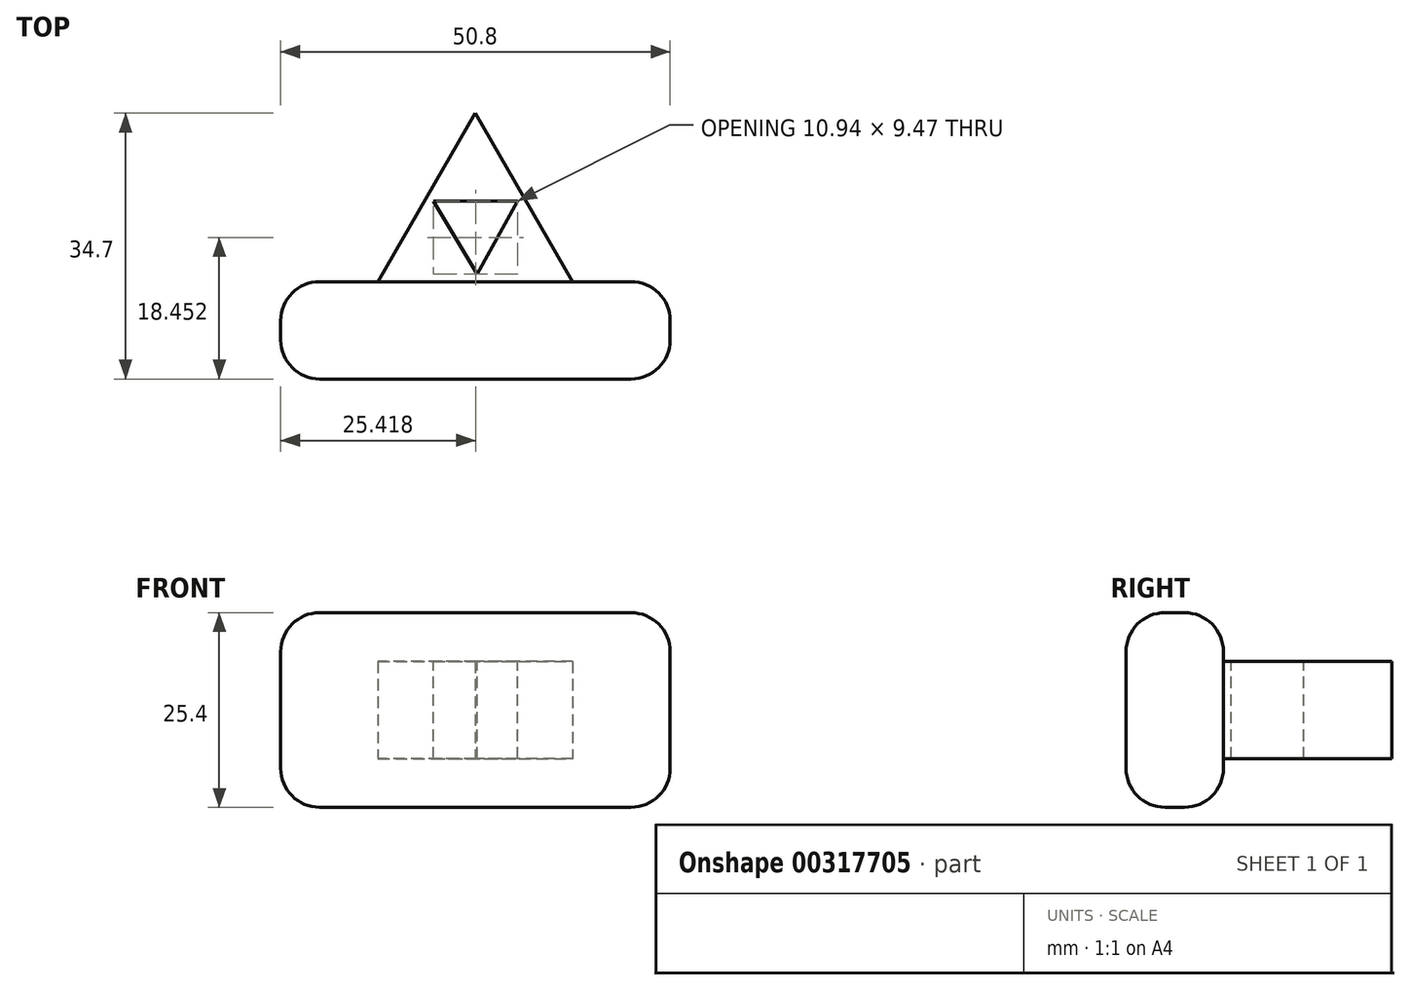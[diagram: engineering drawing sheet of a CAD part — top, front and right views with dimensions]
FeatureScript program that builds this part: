
annotation { "Feature Type Name" : "Feature", "Feature Type Description" : "" }
export const myFeature = defineFeature(function(context is Context, id is Id, definition is map)
    precondition{}
    {
        {
            var Q0;
            Q0=qCreatedBy(makeId("Top.planeOp"),FACE);
            var sketch = newSketch(context, id + "F0", { "sketchPlane" : qUnion([Q0])});
            skLineSegment(sketch, "E0", {"start": v(-12.7, -2.56) * mm, "end": v(12.7, -2.56) * mm});
            skLineSegment(sketch, "E1", {"start": v(12.7, -2.56) * mm, "end": v(0, 19.44) * mm});
            skLineSegment(sketch, "E2", {"start": v(0, 19.44) * mm, "end": v(-12.7, -2.56) * mm});
            skLineSegment(sketch, "E3", {"start": v(-12.7, -2.56) * mm, "end": v(-25.4, -2.56) * mm});
            skLineSegment(sketch, "E4", {"start": v(12.7, -2.56) * mm, "end": v(0.27, -2.56) * mm});
            skLineSegment(sketch, "E5", {"start": v(12.7, -2.56) * mm, "end": v(25.4, -2.56) * mm});
            skLineSegment(sketch, "E6", {"start": v(25.4, -2.56) * mm, "end": v(25.4, -15.26) * mm});
            skLineSegment(sketch, "E7", {"start": v(25.4, -15.26) * mm, "end": v(-25.4, -15.26) * mm});
            skLineSegment(sketch, "E8", {"start": v(-25.4, -15.26) * mm, "end": v(-25.4, -2.56) * mm});
            skLineSegment(sketch, "E9", {"start": v(0.27, -2.56) * mm, "end": v(-6.35, 8.44) * mm});
            skLineSegment(sketch, "E10", {"start": v(-6.35, 8.44) * mm, "end": v(6.35, 8.44) * mm});
            skLineSegment(sketch, "E11", {"start": v(6.35, 8.44) * mm, "end": v(0.27, -2.56) * mm});
            skSolve(sketch);
        }
        {
            var Q0;
            {var subQ0=sQuery(id+"F0.wireOp",EDGE,"E3");Q0=makeQuery(id+"F0.imprint","IMPRINT",FACE,{"disambiguationData":[TD([[makeQuery(id+"F0.imprint","IMPRINT",EDGE,{"derivedFrom":subQ0}),1.0]])]});}
            extrude(context, id + "F1", {"entities" : qUnion([Q0]), "endBound" : BoundingType.SYMMETRIC, "depth" : 25.4 * mm});
        }
        {
            var Q0;
            {var subQ0=sQuery(id+"F0.wireOp",EDGE,"Tj1eZWaM-Gulq-bYq7-VJs6-khO5uOkBsyRu");var subQ1=makeQuery(id+"F0.imprint","INTERSECT",VERTEX,{"derivedFrom":[subQ0,sQuery(id+"F0.wireOp",EDGE,"O4c9BBUU-3zct-c9Sw-KlaS-YK3NOOpSQY2o")]});Q0=makeQuery(id+"F0.imprint","IMPRINT",FACE,{"disambiguationData":[TD([[makeQuery(id+"F0.imprint","IMPRINT",EDGE,{"disambiguationData":[TD([[subQ1,-1.0]])],"derivedFrom":subQ0}),1.0]])]});}
            var Q1;
            {var subQ0=sQuery(id+"F0.wireOp",EDGE,"a1eElIkU-YqGh-bzyB-efgw-AKLIKMZRUDvv");var subQ1=makeQuery(id+"F0.imprint","INTERSECT",VERTEX,{"derivedFrom":[subQ0,sQuery(id+"F0.wireOp",EDGE,"aCEfMeAe-Svce-cfmh-0oVG-zig3SBFzQLm0")]});Q1=makeQuery(id+"F0.imprint","IMPRINT",FACE,{"disambiguationData":[TD([[makeQuery(id+"F0.imprint","IMPRINT",EDGE,{"disambiguationData":[TD([[subQ1,1.0]])],"derivedFrom":subQ0}),1.0]])]});}
            var Q2;
            {var subQ0=sQuery(id+"F0.wireOp",EDGE,"ItRLwo8X-6uFx-N78e-3Ld0-RcMtCkm3otu3");var subQ1=makeQuery(id+"F0.imprint","INTERSECT",VERTEX,{"derivedFrom":[subQ0,sQuery(id+"F0.wireOp",EDGE,"aCEfMeAe-Svce-cfmh-0oVG-zig3SBFzQLm0")]});Q2=makeQuery(id+"F0.imprint","IMPRINT",FACE,{"disambiguationData":[TD([[makeQuery(id+"F0.imprint","IMPRINT",EDGE,{"disambiguationData":[TD([[subQ1,-1.0]])],"derivedFrom":subQ0}),1.0]])]});}
            var Q3;
            {var subQ0=sQuery(id+"F0.wireOp",EDGE,"E4");Q3=makeQuery(id+"F0.imprint","IMPRINT",FACE,{"disambiguationData":[TD([[makeQuery(id+"F0.imprint","IMPRINT",EDGE,{"derivedFrom":subQ0}),-1.0]])]});}
            var Q4;
            {var subQ0=sQuery(id+"F0.wireOp",EDGE,"E0");Q4=makeQuery(id+"F0.imprint","IMPRINT",FACE,{"disambiguationData":[TD([[makeQuery(id+"F0.imprint","IMPRINT",EDGE,{"derivedFrom":subQ0}),1.0]])]});}
            var Q5;
            {var subQ3=sQuery(id+"F0.wireOp",EDGE,"E10");Q5=makeQuery(id+"F0.imprint","IMPRINT",FACE,{"disambiguationData":[TD([[makeQuery(id+"F0.imprint","IMPRINT",EDGE,{"derivedFrom":subQ3}),1.0]])]});}
            var Q6;
            Q6=makeQuery(id+"F0.imprint","IMPRINT",FACE,{"disambiguationData":[TD([[makeQuery(id+"F0.imprint","IMPRINT",EDGE,{"derivedFrom":sQuery(id+"F0.wireOp",EDGE,"E9")}),-1.0]])]});
            extrude(context, id + "F2", {"entities" : qUnion([Q0, Q1, Q2, Q3, Q4, Q5, Q6]), "operationType" : NewBodyOperationType.ADD, "endBound" : BoundingType.SYMMETRIC, "depth" : 12.7 * mm});
        }
        {
            var Q0;
            Q0=makeQuery(id+"F2.opExtrude","CAP_FACE",FACE,{"disambiguationData":[OSD([sQuery(id+"F0.wireOp",EDGE,"E0"),sQuery(id+"F0.wireOp",EDGE,"E1"),sQuery(id+"F0.wireOp",EDGE,"E2"),sQuery(id+"F0.wireOp",EDGE,"E4")])],"isStart":false});
            var sketch = newSketch(context, id + "F3", { "sketchPlane" : qUnion([Q0])});
            skLineSegment(sketch, "E12.0", {"start": v(6.35, 8.44) * mm, "end": v(0.27, -2.56) * mm});
            skLineSegment(sketch, "E13.0", {"start": v(0.27, -2.56) * mm, "end": v(-6.35, 8.44) * mm});
            skLineSegment(sketch, "E14.0", {"start": v(-6.35, 8.44) * mm, "end": v(6.35, 8.44) * mm});
            skLineSegment(sketch, "E15.0", {"start": v(-5.45, 7.93) * mm, "end": v(5.49, 7.93) * mm});
            skLineSegment(sketch, "E15.1", {"start": v(0.25, -1.55) * mm, "end": v(-5.45, 7.93) * mm});
            skLineSegment(sketch, "E15.2", {"start": v(5.49, 7.93) * mm, "end": v(0.25, -1.55) * mm});
            skSolve(sketch);
        }
        {
            var Q0;
            Q0=makeQuery(id+"F3.imprint","IMPRINT",FACE,{"disambiguationData":[TD([[makeQuery(id+"F3.imprint","IMPRINT",EDGE,{"derivedFrom":sQuery(id+"F3.wireOp",EDGE,"E15.0")}),-1.0]])]});
            extrude(context, id + "F4", {"entities" : qUnion([Q0]), "operationType" : NewBodyOperationType.REMOVE, "endBound" : BoundingType.THROUGH_ALL, "oppositeDirection" : true, "depth" : 25.4 * mm});
        }
        {
            var Q0;
            Q0=makeQuery(id+"F1.opExtrude","CAP_EDGE",EDGE,{"disambiguationData":[OSD([sQuery(id+"F0.wireOp",EDGE,"E8")])],"isStart":false});
            var Q1;
            Q1=makeQuery(id+"F1.opExtrude","CAP_EDGE",EDGE,{"disambiguationData":[OSD([sQuery(id+"F0.wireOp",EDGE,"E8")])],"isStart":true});
            var Q2;
            Q2=makeQuery(id+"F1.opExtrude","CAP_EDGE",EDGE,{"disambiguationData":[OSD([sQuery(id+"F0.wireOp",EDGE,"E6")])],"isStart":true});
            var Q3;
            Q3=makeQuery(id+"F1.opExtrude","CAP_EDGE",EDGE,{"disambiguationData":[OSD([sQuery(id+"F0.wireOp",EDGE,"E6")])],"isStart":false});
            var Q4;
            Q4=makeQuery(id+"F1.opExtrude","SWEPT_FACE",FACE,{"disambiguationData":[OSD([sQuery(id+"F0.wireOp",EDGE,"E7")])]});
            var Q5;
            Q5=makeQuery(id+"F1.opExtrude","CAP_EDGE",EDGE,{"disambiguationData":[OSD([sQuery(id+"F0.wireOp",EDGE,"E0"),sQuery(id+"F0.wireOp",EDGE,"E3"),sQuery(id+"F0.wireOp",EDGE,"E4"),sQuery(id+"F0.wireOp",EDGE,"E5")])],"isStart":false});
            var Q6;
            Q6=makeQuery(id+"F1.opExtrude","CAP_FACE",FACE,{"disambiguationData":[OSD([sQuery(id+"F0.wireOp",EDGE,"E0"),sQuery(id+"F0.wireOp",EDGE,"E3"),sQuery(id+"F0.wireOp",EDGE,"E4"),sQuery(id+"F0.wireOp",EDGE,"E5"),sQuery(id+"F0.wireOp",EDGE,"E6"),sQuery(id+"F0.wireOp",EDGE,"E7"),sQuery(id+"F0.wireOp",EDGE,"E8")])],"isStart":true});
            var Q7;
            Q7=makeQuery(id+"F1.opExtrude","SWEPT_EDGE",EDGE,{"disambiguationData":[OSD([sQuery(id+"F0.wireOp",EDGE,"E5"),sQuery(id+"F0.wireOp",EDGE,"E6")])]});
            var Q8;
            Q8=makeQuery(id+"F1.opExtrude","SWEPT_EDGE",EDGE,{"disambiguationData":[OSD([sQuery(id+"F0.wireOp",EDGE,"E3"),sQuery(id+"F0.wireOp",EDGE,"E8")])]});
            fillet(context, id + "F5", {"entities" : qUnion([Q0, Q1, Q2, Q3, Q4, Q5, Q6, Q7, Q8]), "radius" : 5.08 * mm, "tangentPropagation" : true, "allowEdgeOverflow" : false});
        }
    });
